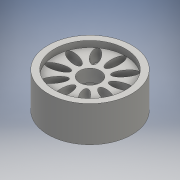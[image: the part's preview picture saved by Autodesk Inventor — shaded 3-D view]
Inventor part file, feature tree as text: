
AUTODESK INVENTOR PART (.ipt)
format: ipt  version: 2016 (Build 200138000, 138)  size: 198,656 bytes
history: native  units: mm
features: extrude x4, sketch x2, projected_geometry x2, other x1
ambient origin geometry x8: Origin, YZ Plane, XZ Plane, XY Plane, X Axis, Y Axis, Z Axis, Center Point
bodies: Body1 (feature_tree)
feature tree (9):
  other  "ソリッド1"
  sketch  "スケッチ1"
  extrude  "押し出し1"  Depth=20.0mm
  extrude  "押し出し2"  Depth=11.6mm
  sketch  "スケッチ2"
  extrude  "押し出し3"  Depth=8.5mm TaperAngle=0.0deg
  extrude  "押し出し4"  Depth=4.0mm TaperAngle=0.0deg
  projected_geometry  "投影ループ1"
  projected_geometry  "投影ループ2"
